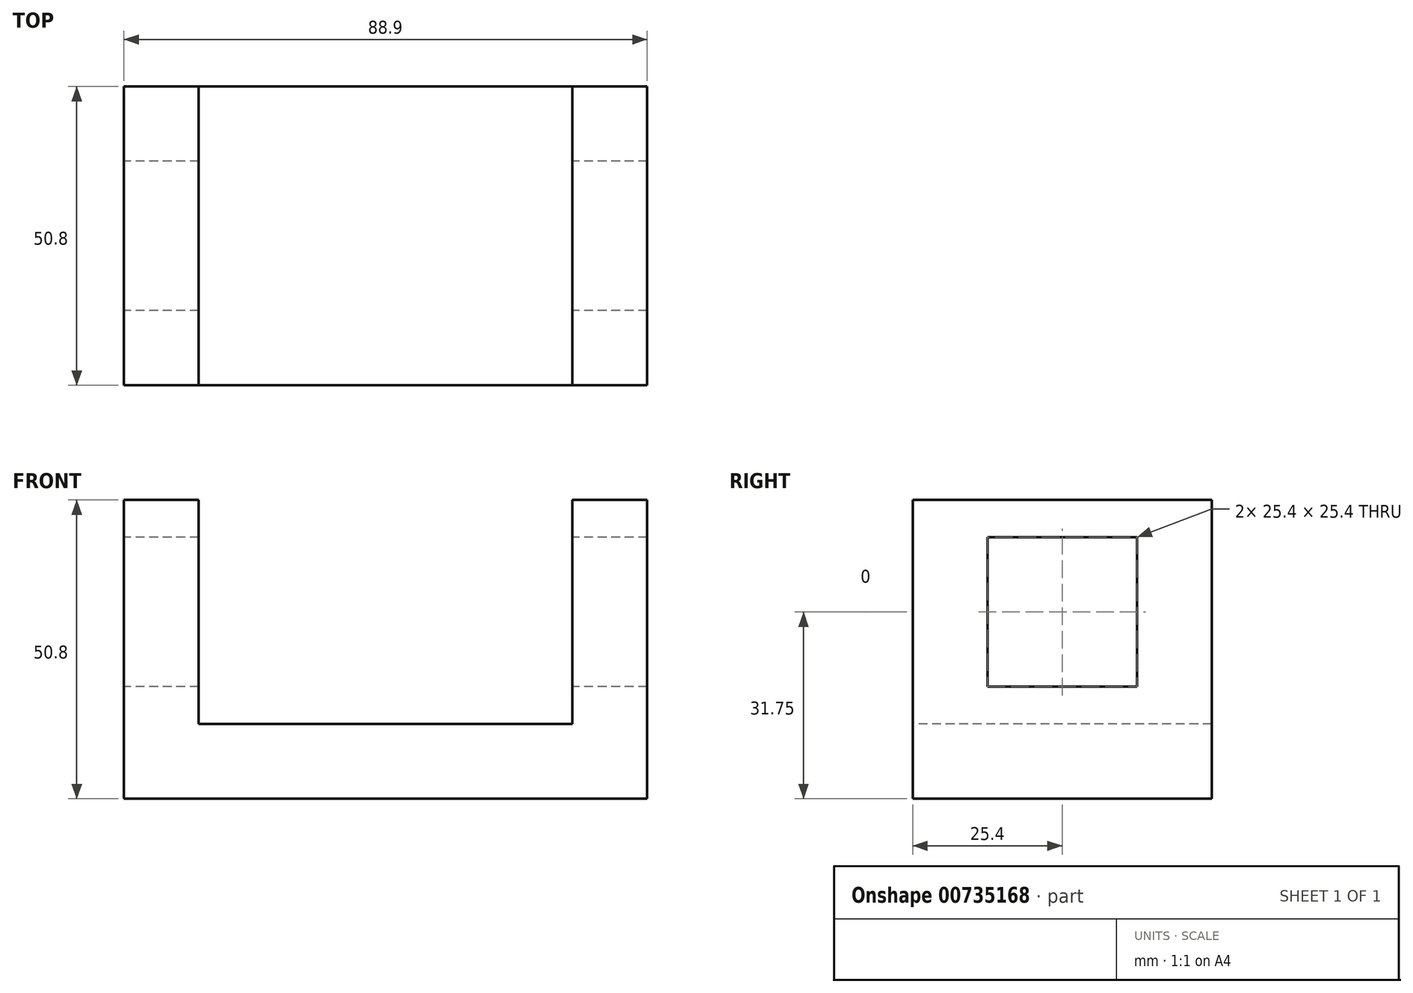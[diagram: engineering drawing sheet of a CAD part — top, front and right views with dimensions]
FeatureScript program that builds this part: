
annotation { "Feature Type Name" : "Feature", "Feature Type Description" : "" }
export const myFeature = defineFeature(function(context is Context, id is Id, definition is map)
    precondition{}
    {
        {
            var Q0;
            Q0=qCreatedBy(makeId("Right.planeOp"),FACE);
            var sketch = newSketch(context, id + "F0", { "sketchPlane" : qUnion([Q0])});
            skLineSegment(sketch, "E0.bottom", {"start": v(-25.4, 25.4) * mm, "end": v(25.4, 25.4) * mm});
            skLineSegment(sketch, "E0.top", {"start": v(-25.4, -25.4) * mm, "end": v(25.4, -25.4) * mm});
            skLineSegment(sketch, "E0.left", {"start": v(-25.4, 25.4) * mm, "end": v(-25.4, -25.4) * mm});
            skLineSegment(sketch, "E0.right", {"start": v(25.4, 25.4) * mm, "end": v(25.4, -25.4) * mm});
            skPoint(sketch, "E0.middle", {"position": v(0, 0) * mm});
            skPoint(sketch, "E1.left.end.orphan", {"position": v(-263.44, 16.4) * mm});
            skPoint(sketch, "E1.right.end.orphan", {"position": v(199.7, -113.64) * mm});
            skPoint(sketch, "E1.bottom.end.orphan", {"position": v(263.44, -16.4) * mm});
            skPoint(sketch, "E1.bottom.start.orphan", {"position": v(-199.7, 113.64) * mm});
            skLineSegment(sketch, "E2.bottom", {"start": v(-12.7, 19.05) * mm, "end": v(12.7, 19.05) * mm});
            skLineSegment(sketch, "E2.top", {"start": v(-12.7, -6.35) * mm, "end": v(12.7, -6.35) * mm});
            skLineSegment(sketch, "E2.left", {"start": v(-12.7, 19.05) * mm, "end": v(-12.7, -6.35) * mm});
            skLineSegment(sketch, "E2.right", {"start": v(12.7, 19.05) * mm, "end": v(12.7, -6.35) * mm});
            skSolve(sketch);
        }
        {
            var Q0;
            Q0=makeQuery(id+"F0.imprint","IMPRINT",FACE,{"disambiguationData":[TD([[makeQuery(id+"F0.imprint","IMPRINT",EDGE,{"derivedFrom":sQuery(id+"F0.wireOp",EDGE,"E0.bottom")}),-1.0]])]});
            extrude(context, id + "F1", {"entities" : qUnion([Q0]), "depth" : 88.9 * mm, "offsetDistance" : 25.4 * mm});
        }
        {
            var Q0;
            Q0=makeQuery(id+"F1.opExtrude","SWEPT_FACE",FACE,{"disambiguationData":[OSD([sQuery(id+"F0.wireOp",EDGE,"E0.left")])]});
            var sketch = newSketch(context, id + "F2", { "sketchPlane" : qUnion([Q0])});
            skLineSegment(sketch, "E3.top", {"start": v(12.7, -12.7) * mm, "end": v(76.2, -12.7) * mm});
            skLineSegment(sketch, "E3.left", {"start": v(12.7, 25.4) * mm, "end": v(12.7, -12.7) * mm});
            skLineSegment(sketch, "E3.right", {"start": v(76.2, 25.4) * mm, "end": v(76.2, -12.7) * mm});
            skPoint(sketch, "E3.middle", {"position": v(44.45, 6.35) * mm});
            skSolve(sketch);
        }
        {
            var Q0;
            Q0=makeQuery(id+"F2.imprint","IMPRINT",FACE,{"disambiguationData":[TD([[makeQuery(id+"F2.imprint","IMPRINT",EDGE,{"derivedFrom":sQuery(id+"F2.wireOp",EDGE,"E3.top")}),1.0]])]});
            extrude(context, id + "F3", {"entities" : qUnion([Q0]), "operationType" : NewBodyOperationType.REMOVE, "oppositeDirection" : true, "depth" : 50.8 * mm, "offsetDistance" : 25.4 * mm});
        }
    });
